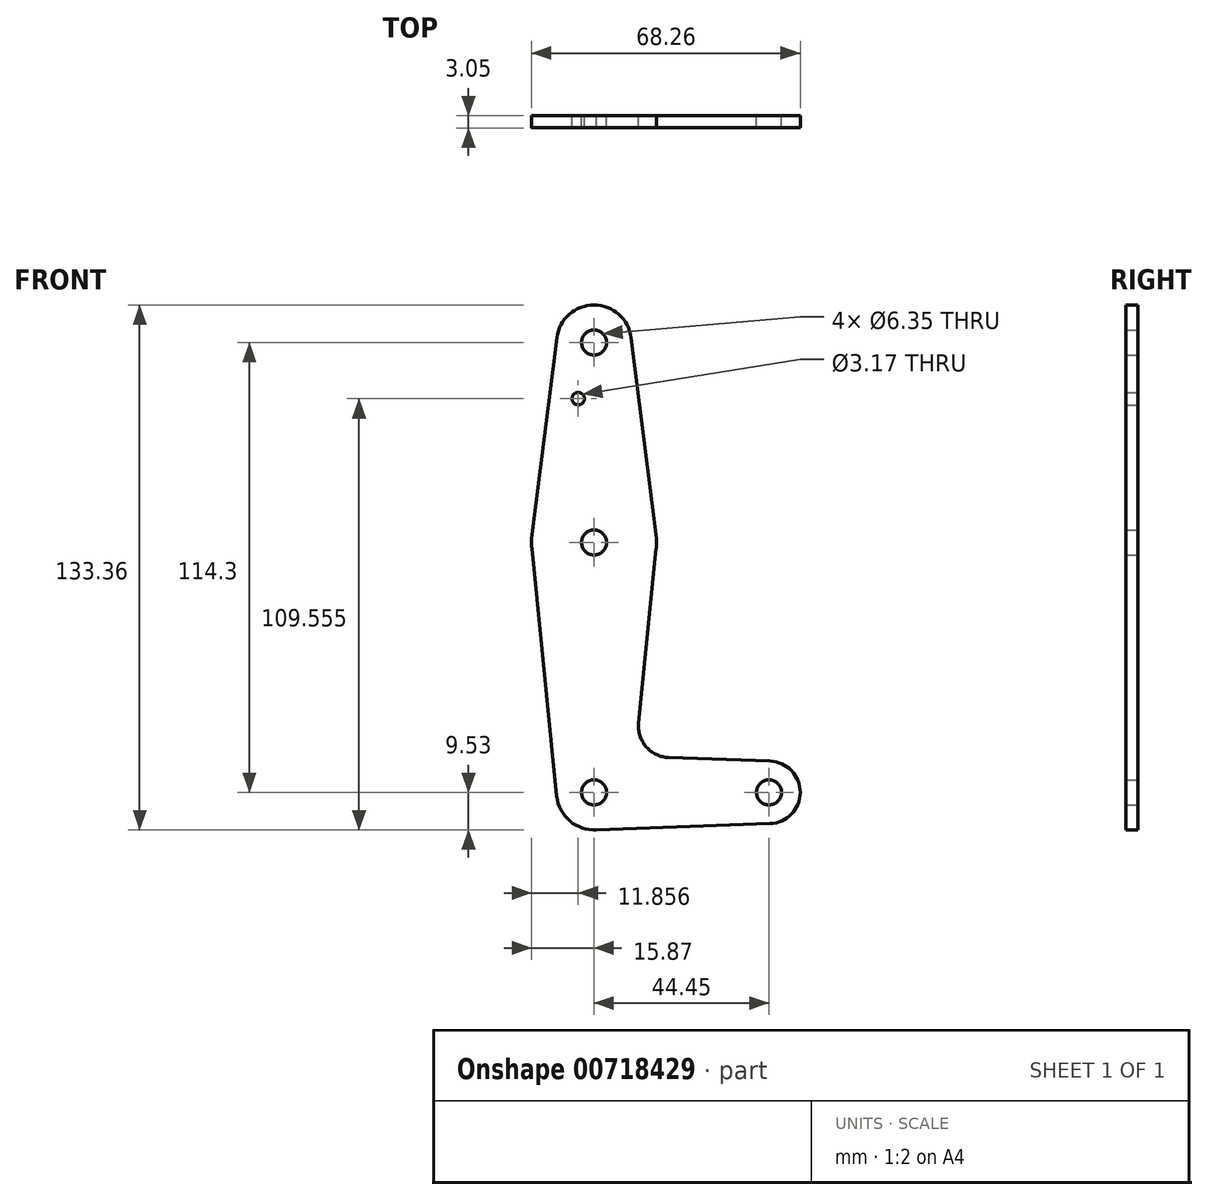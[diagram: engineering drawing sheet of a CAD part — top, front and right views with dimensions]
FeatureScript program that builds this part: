
annotation { "Feature Type Name" : "Feature", "Feature Type Description" : "" }
export const myFeature = defineFeature(function(context is Context, id is Id, definition is map)
    precondition{}
    {
        {
            var Q0;
            Q0=qCreatedBy(makeId("Front.planeOp"),FACE);
            var sketch = newSketch(context, id + "F0", { "sketchPlane" : qUnion([Q0])});
            skCircle(sketch, "E0", {"center": v(0, 0) * mm, "radius": 9.52 * mm});
            skLineSegment(sketch, "E1", {"start": v(0, 0) * mm, "end": v(0, 114.3) * mm});
            skCircle(sketch, "E2", {"center": v(0, 114.3) * mm, "radius": 9.53 * mm});
            skCircle(sketch, "E3", {"center": v(0, 63.5) * mm, "radius": 15.88 * mm});
            skLineSegment(sketch, "E4", {"start": v(0, 0) * mm, "end": v(44.45, 0) * mm});
            skCircle(sketch, "E5", {"center": v(44.45, 0) * mm, "radius": 7.94 * mm});
            skLineSegment(sketch, "E6", {"start": v(-9.45, 115.5) * mm, "end": v(-15.75, 65.48) * mm});
            skLineSegment(sketch, "E7", {"start": v(9.45, 115.5) * mm, "end": v(15.75, 65.48) * mm});
            skLineSegment(sketch, "E8", {"start": v(15.8, 61.91) * mm, "end": v(11.34, 17.59) * mm});
            skLineSegment(sketch, "E9", {"start": v(0, -9.52) * mm, "end": v(44.73, -7.93) * mm});
            skLineSegment(sketch, "E10", {"start": v(-15.8, 61.91) * mm, "end": v(-9.48, -0.95) * mm});
            skLineSegment(sketch, "E11", {"start": v(18.97, 8.85) * mm, "end": v(44.73, 7.93) * mm});
            skArc(sketch, "E12.filletArc", {"start": v(11.34, 17.59) * mm, "mid": v(13.26, 11.57) * mm, "end": v(18.97, 8.85) * mm});
            skCircle(sketch, "E13", {"center": v(0, 114.3) * mm, "radius": 3.18 * mm});
            skCircle(sketch, "E14", {"center": v(0, 63.5) * mm, "radius": 3.18 * mm});
            skCircle(sketch, "E15", {"center": v(0, 0) * mm, "radius": 3.18 * mm});
            skCircle(sketch, "E16", {"center": v(44.45, 0) * mm, "radius": 3.18 * mm});
            skCircle(sketch, "E17", {"center": v(-4.01, 100.03) * mm, "radius": 1.59 * mm});
            skSolve(sketch);
        }
        {
            var Q0;
            Q0 = qSketchRegion(id + "F0", true);
            var Q1;
            {var subQ0=sQuery(id+"F0.wireOp",EDGE,"E1");var subQ1=sQuery(id+"F0.wireOp",EDGE,"E0");var subQ2=makeQuery(id+"F0.imprint","INTERSECT",VERTEX,{"derivedFrom":[subQ1,subQ0]});Q1=makeQuery(id+"F0.imprint","IMPRINT",FACE,{"disambiguationData":[TD([[makeQuery(id+"F0.imprint","IMPRINT",EDGE,{"disambiguationData":[TD([[subQ2,1.0]])],"derivedFrom":subQ1}),1.0]])]});}
            extrude(context, id + "F1", {"entities" : qUnion([Q0, Q1]), "depth" : 3.05 * mm, "offsetDistance" : 25.4 * mm});
        }
    });
